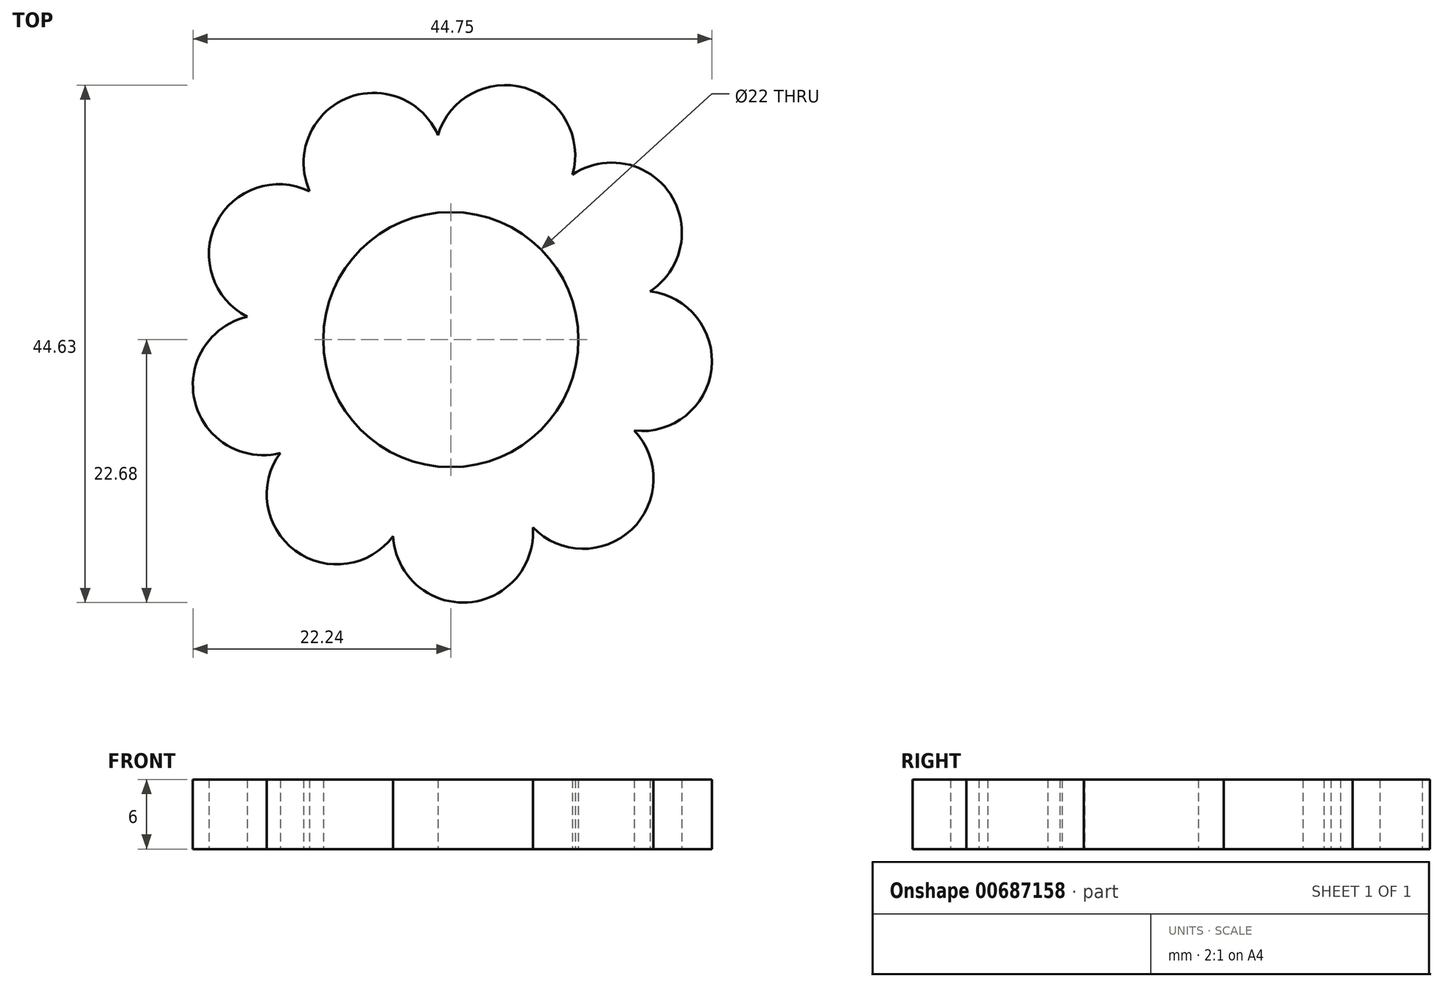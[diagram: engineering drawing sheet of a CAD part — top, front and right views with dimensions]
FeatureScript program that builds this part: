
annotation { "Feature Type Name" : "Feature", "Feature Type Description" : "" }
export const myFeature = defineFeature(function(context is Context, id is Id, definition is map)
    precondition{}
    {
        {
            var Q0;
            Q0=qCreatedBy(makeId("Top.planeOp"),FACE);
            var sketch = newSketch(context, id + "F0", { "sketchPlane" : qUnion([Q0])});
            skCircle(sketch, "E0", {"center": v(0, 0) * mm, "radius": 11 * mm});
            skLineSegment(sketch, "E1.0", {"start": v(15.82, -7.85) * mm, "end": v(7.07, -16.19) * mm});
            skLineSegment(sketch, "E1.1", {"start": v(7.07, -16.19) * mm, "end": v(-4.99, -16.95) * mm});
            skLineSegment(sketch, "E1.2", {"start": v(-4.99, -16.95) * mm, "end": v(-14.71, -9.78) * mm});
            skLineSegment(sketch, "E1.3", {"start": v(-14.71, -9.78) * mm, "end": v(-17.55, 1.97) * mm});
            skLineSegment(sketch, "E1.4", {"start": v(-17.55, 1.97) * mm, "end": v(-12.18, 12.8) * mm});
            skLineSegment(sketch, "E1.5", {"start": v(-12.18, 12.8) * mm, "end": v(-1.11, 17.63) * mm});
            skLineSegment(sketch, "E1.6", {"start": v(-1.11, 17.63) * mm, "end": v(10.48, 14.22) * mm});
            skLineSegment(sketch, "E1.7", {"start": v(10.48, 14.22) * mm, "end": v(17.17, 4.16) * mm});
            skLineSegment(sketch, "E1.8", {"start": v(17.17, 4.16) * mm, "end": v(15.82, -7.85) * mm});
            skPoint(sketch, "E1.0.midPoint", {"position": v(11.45, -12.02) * mm});
            skArc(sketch, "E2", {"start": v(10.48, 14.22) * mm, "mid": v(6.38, 21.7) * mm, "end": v(-1.11, 17.63) * mm});
            skArc(sketch, "E3", {"start": v(17.17, 4.16) * mm, "mid": v(18.91, 12.57) * mm, "end": v(10.48, 14.22) * mm});
            skArc(sketch, "E4", {"start": v(15.82, -7.85) * mm, "mid": v(22.47, -2.52) * mm, "end": v(17.17, 4.16) * mm});
            skArc(sketch, "E5", {"start": v(7.07, -16.19) * mm, "mid": v(15.6, -16.37) * mm, "end": v(15.82, -7.85) * mm});
            skArc(sketch, "E6", {"start": v(-4.99, -16.95) * mm, "mid": v(1.43, -22.66) * mm, "end": v(7.07, -16.19) * mm});
            skArc(sketch, "E7", {"start": v(-14.71, -9.78) * mm, "mid": v(-13.42, -18.2) * mm, "end": v(-4.99, -16.95) * mm});
            skArc(sketch, "E8", {"start": v(-17.55, 1.97) * mm, "mid": v(-22.07, -5.34) * mm, "end": v(-14.71, -9.78) * mm});
            skArc(sketch, "E9", {"start": v(-12.18, 12.8) * mm, "mid": v(-20.23, 10.04) * mm, "end": v(-17.55, 1.97) * mm});
            skArc(sketch, "E10", {"start": v(-1.11, 17.63) * mm, "mid": v(-9.08, 20.77) * mm, "end": v(-12.18, 12.8) * mm});
            skSolve(sketch);
        }
        {
            var Q0;
            Q0=makeQuery(id+"F0.imprint","IMPRINT",FACE,{"disambiguationData":[TD([[makeQuery(id+"F0.imprint","IMPRINT",EDGE,{"derivedFrom":sQuery(id+"F0.wireOp",EDGE,"E0")}),-1.0]])]});
            var Q1;
            Q1=makeQuery(id+"F0.imprint","IMPRINT",FACE,{"disambiguationData":[TD([[makeQuery(id+"F0.imprint","IMPRINT",EDGE,{"derivedFrom":sQuery(id+"F0.wireOp",EDGE,"E1.6")}),1.0]])]});
            var Q2;
            Q2=makeQuery(id+"F0.imprint","IMPRINT",FACE,{"disambiguationData":[TD([[makeQuery(id+"F0.imprint","IMPRINT",EDGE,{"derivedFrom":sQuery(id+"F0.wireOp",EDGE,"E1.5")}),1.0]])]});
            var Q3;
            Q3=makeQuery(id+"F0.imprint","IMPRINT",FACE,{"disambiguationData":[TD([[makeQuery(id+"F0.imprint","IMPRINT",EDGE,{"derivedFrom":sQuery(id+"F0.wireOp",EDGE,"E1.4")}),1.0]])]});
            var Q4;
            Q4=makeQuery(id+"F0.imprint","IMPRINT",FACE,{"disambiguationData":[TD([[makeQuery(id+"F0.imprint","IMPRINT",EDGE,{"derivedFrom":sQuery(id+"F0.wireOp",EDGE,"E1.3")}),1.0]])]});
            var Q5;
            Q5=makeQuery(id+"F0.imprint","IMPRINT",FACE,{"disambiguationData":[TD([[makeQuery(id+"F0.imprint","IMPRINT",EDGE,{"derivedFrom":sQuery(id+"F0.wireOp",EDGE,"E1.2")}),1.0]])]});
            var Q6;
            Q6=makeQuery(id+"F0.imprint","IMPRINT",FACE,{"disambiguationData":[TD([[makeQuery(id+"F0.imprint","IMPRINT",EDGE,{"derivedFrom":sQuery(id+"F0.wireOp",EDGE,"E1.1")}),1.0]])]});
            var Q7;
            Q7=makeQuery(id+"F0.imprint","IMPRINT",FACE,{"disambiguationData":[TD([[makeQuery(id+"F0.imprint","IMPRINT",EDGE,{"derivedFrom":sQuery(id+"F0.wireOp",EDGE,"E1.0")}),1.0]])]});
            var Q8;
            Q8=makeQuery(id+"F0.imprint","IMPRINT",FACE,{"disambiguationData":[TD([[makeQuery(id+"F0.imprint","IMPRINT",EDGE,{"derivedFrom":sQuery(id+"F0.wireOp",EDGE,"E1.8")}),1.0]])]});
            var Q9;
            Q9=makeQuery(id+"F0.imprint","IMPRINT",FACE,{"disambiguationData":[TD([[makeQuery(id+"F0.imprint","IMPRINT",EDGE,{"derivedFrom":sQuery(id+"F0.wireOp",EDGE,"E1.7")}),1.0]])]});
            extrude(context, id + "F1", {"entities" : qUnion([Q0, Q1, Q2, Q3, Q4, Q5, Q6, Q7, Q8, Q9]), "depth" : 6 * mm, "offsetDistance" : 25 * mm});
        }
    });
